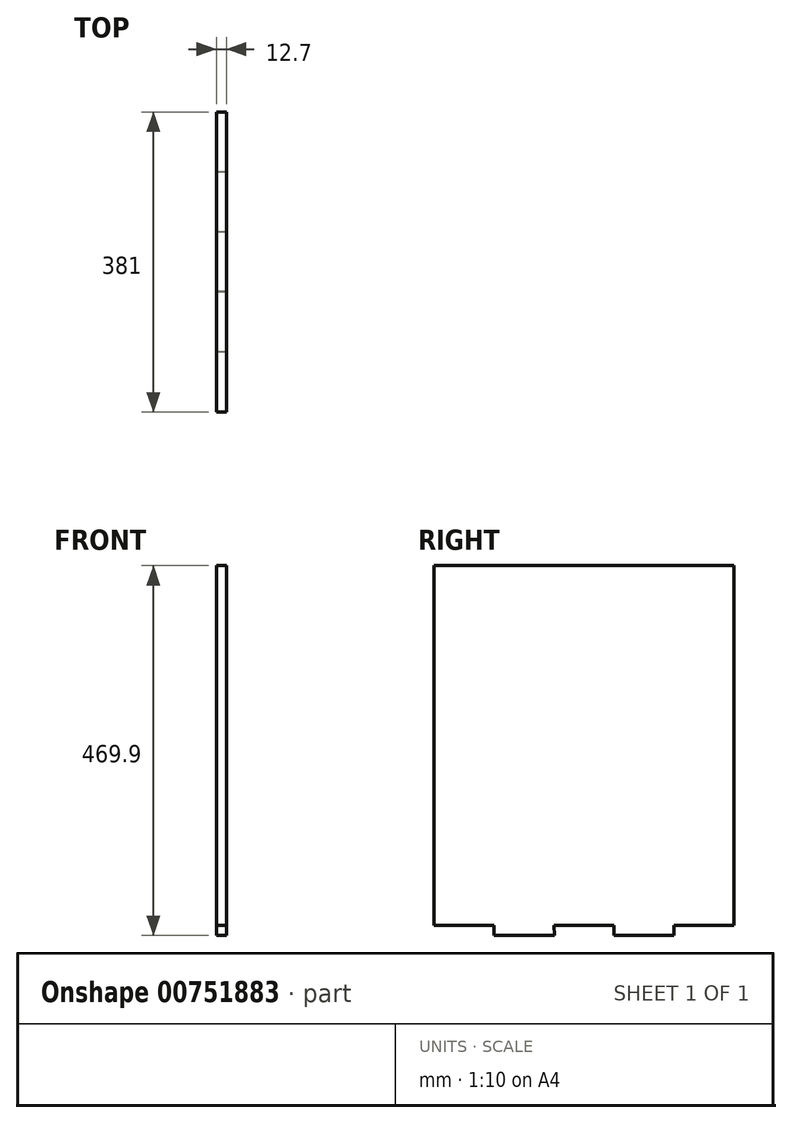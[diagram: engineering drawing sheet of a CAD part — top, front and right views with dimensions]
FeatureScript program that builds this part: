
annotation { "Feature Type Name" : "Feature", "Feature Type Description" : "" }
export const myFeature = defineFeature(function(context is Context, id is Id, definition is map)
    precondition{}
    {
        {
            var Q0;
            Q0=qCreatedBy(makeId("Right.planeOp"),FACE);
            var sketch = newSketch(context, id + "F0", { "sketchPlane" : qUnion([Q0])});
            skLineSegment(sketch, "E0.bottom", {"start": v(-186.87, 161.3) * mm, "end": v(194.13, 161.3) * mm});
            skLineSegment(sketch, "E0.top", {"start": v(-186.87, -295.9) * mm, "end": v(-110.67, -295.9) * mm});
            skLineSegment(sketch, "E0.left", {"start": v(-186.87, 161.3) * mm, "end": v(-186.87, -295.9) * mm});
            skLineSegment(sketch, "E0.right", {"start": v(194.13, 161.3) * mm, "end": v(194.13, -295.9) * mm});
            skLineSegment(sketch, "E1", {"start": v(-110.67, -295.9) * mm, "end": v(-110.67, -308.6) * mm});
            skLineSegment(sketch, "E2", {"start": v(-110.67, -308.6) * mm, "end": v(-33.8, -308.6) * mm});
            skLineSegment(sketch, "E3", {"start": v(-33.8, -308.6) * mm, "end": v(-34.47, -295.9) * mm});
            skLineSegment(sketch, "E4", {"start": v(41.73, -295.9) * mm, "end": v(41.73, -308.6) * mm});
            skLineSegment(sketch, "E5", {"start": v(41.73, -308.6) * mm, "end": v(117.93, -308.6) * mm});
            skLineSegment(sketch, "E6", {"start": v(117.93, -308.6) * mm, "end": v(117.93, -295.9) * mm});
            skLineSegment(sketch, "E7.trimOffspring", {"start": v(-34.47, -295.9) * mm, "end": v(41.73, -295.9) * mm});
            skLineSegment(sketch, "E8.trimOffspring", {"start": v(117.93, -295.9) * mm, "end": v(194.13, -295.9) * mm});
            skSolve(sketch);
        }
        {
            var Q0;
            Q0=qSketchRegion(id+"F0",true);
            extrude(context, id + "F1", {"entities" : qUnion([Q0]), "depth" : 12.7 * mm, "offsetDistance" : 25.4 * mm});
        }
    });
